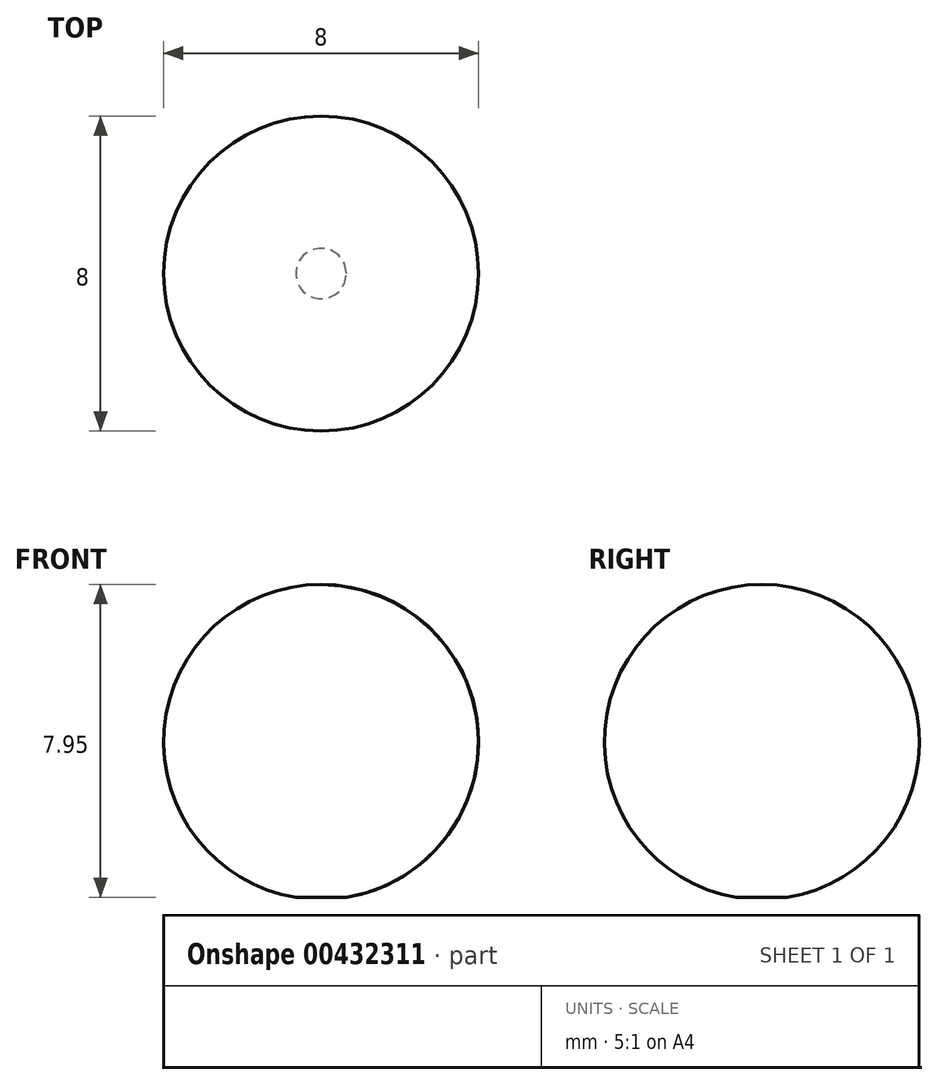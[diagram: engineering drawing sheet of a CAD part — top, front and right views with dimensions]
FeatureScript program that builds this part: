
annotation { "Feature Type Name" : "Feature", "Feature Type Description" : "" }
export const myFeature = defineFeature(function(context is Context, id is Id, definition is map)
    precondition{}
    {
        {
            var Q0;
            Q0=qCreatedBy(makeId("Front.planeOp"),FACE);
            var sketch = newSketch(context, id + "F0", { "sketchPlane" : qUnion([Q0])});
            skArc(sketch, "E0", {"start": v(0.64, -3.95) * mm, "mid": v(3.99, 0.32) * mm, "end": v(0, 4) * mm});
            skLineSegment(sketch, "E1", {"start": v(0, 4) * mm, "end": v(0, -3.95) * mm});
            skLineSegment(sketch, "E2", {"start": v(0, -3.95) * mm, "end": v(0.64, -3.95) * mm});
            skSolve(sketch);
        }
        {
            var Q0;
            Q0=makeQuery(id+"F0.imprint","IMPRINT",FACE,{"disambiguationData":[TD([[makeQuery(id+"F0.imprint","IMPRINT",EDGE,{"derivedFrom":sQuery(id+"F0.wireOp",EDGE,"E0")}),1.0]])]});
            var Q1;
            Q1=sQuery(id+"F0.wireOp",EDGE,"E1");
            revolve(context, id + "F1", {"entities" : qUnion([Q0]), "axis" : qUnion([Q1]), "revolveType" : RevolveType.FULL});
        }
    });
